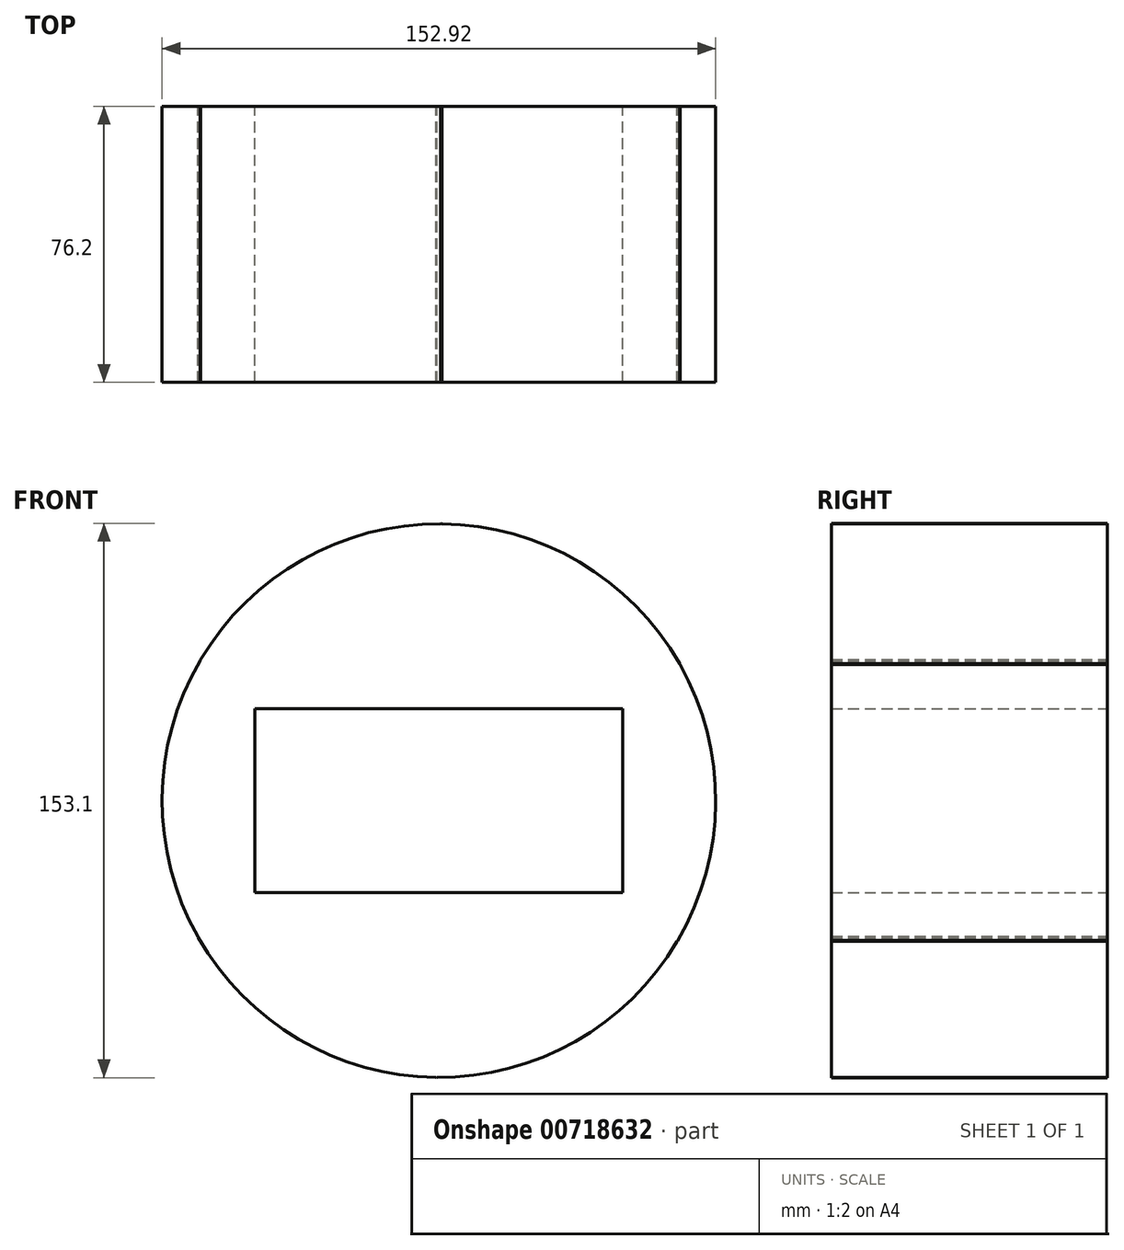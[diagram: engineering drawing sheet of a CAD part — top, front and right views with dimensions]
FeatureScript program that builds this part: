
annotation { "Feature Type Name" : "Feature", "Feature Type Description" : "" }
export const myFeature = defineFeature(function(context is Context, id is Id, definition is map)
    precondition{}
    {
        {
            var Q0;
            Q0=qCreatedBy(makeId("Front.planeOp"),FACE);
            var sketch = newSketch(context, id + "F0", { "sketchPlane" : qUnion([Q0])});
            skLineSegment(sketch, "E0.bottom", {"start": v(50.8, 25.4) * mm, "end": v(-50.8, 25.4) * mm});
            skLineSegment(sketch, "E0.top", {"start": v(50.8, -25.4) * mm, "end": v(-50.8, -25.4) * mm});
            skLineSegment(sketch, "E0.left", {"start": v(50.8, 25.4) * mm, "end": v(50.8, -25.4) * mm});
            skLineSegment(sketch, "E0.right", {"start": v(-50.8, 25.4) * mm, "end": v(-50.8, -25.4) * mm});
            skPoint(sketch, "E0.middle", {"position": v(0, 0) * mm});
            skCircle(sketch, "E1", {"center": v(0, 0) * mm, "radius": 76.46 * mm});
            skCircle(sketch, "E2.cCircle", {"center": v(0, 0) * mm, "radius": 66.3 * mm, "construction": true});
            skLineSegment(sketch, "E2.0", {"start": v(0.65, 76.55) * mm, "end": v(66.62, 37.71) * mm});
            skLineSegment(sketch, "E2.1", {"start": v(66.62, 37.71) * mm, "end": v(65.97, -38.84) * mm});
            skLineSegment(sketch, "E2.2", {"start": v(65.97, -38.84) * mm, "end": v(-0.65, -76.55) * mm});
            skLineSegment(sketch, "E2.3", {"start": v(-0.65, -76.55) * mm, "end": v(-66.62, -37.71) * mm});
            skLineSegment(sketch, "E2.4", {"start": v(-66.62, -37.71) * mm, "end": v(-65.97, 38.84) * mm});
            skLineSegment(sketch, "E2.5", {"start": v(-65.97, 38.84) * mm, "end": v(0.65, 76.55) * mm});
            skPoint(sketch, "E2.0.midPoint", {"position": v(33.64, 57.13) * mm});
            skSolve(sketch);
        }
        {
            var Q0;
            Q0 = qSketchRegion(id + "F0", true);
            extrude(context, id + "F1", {"entities" : qUnion([Q0]), "endBound" : BoundingType.SYMMETRIC, "depth" : 76.2 * mm, "offsetDistance" : 25.4 * mm});
        }
    });
